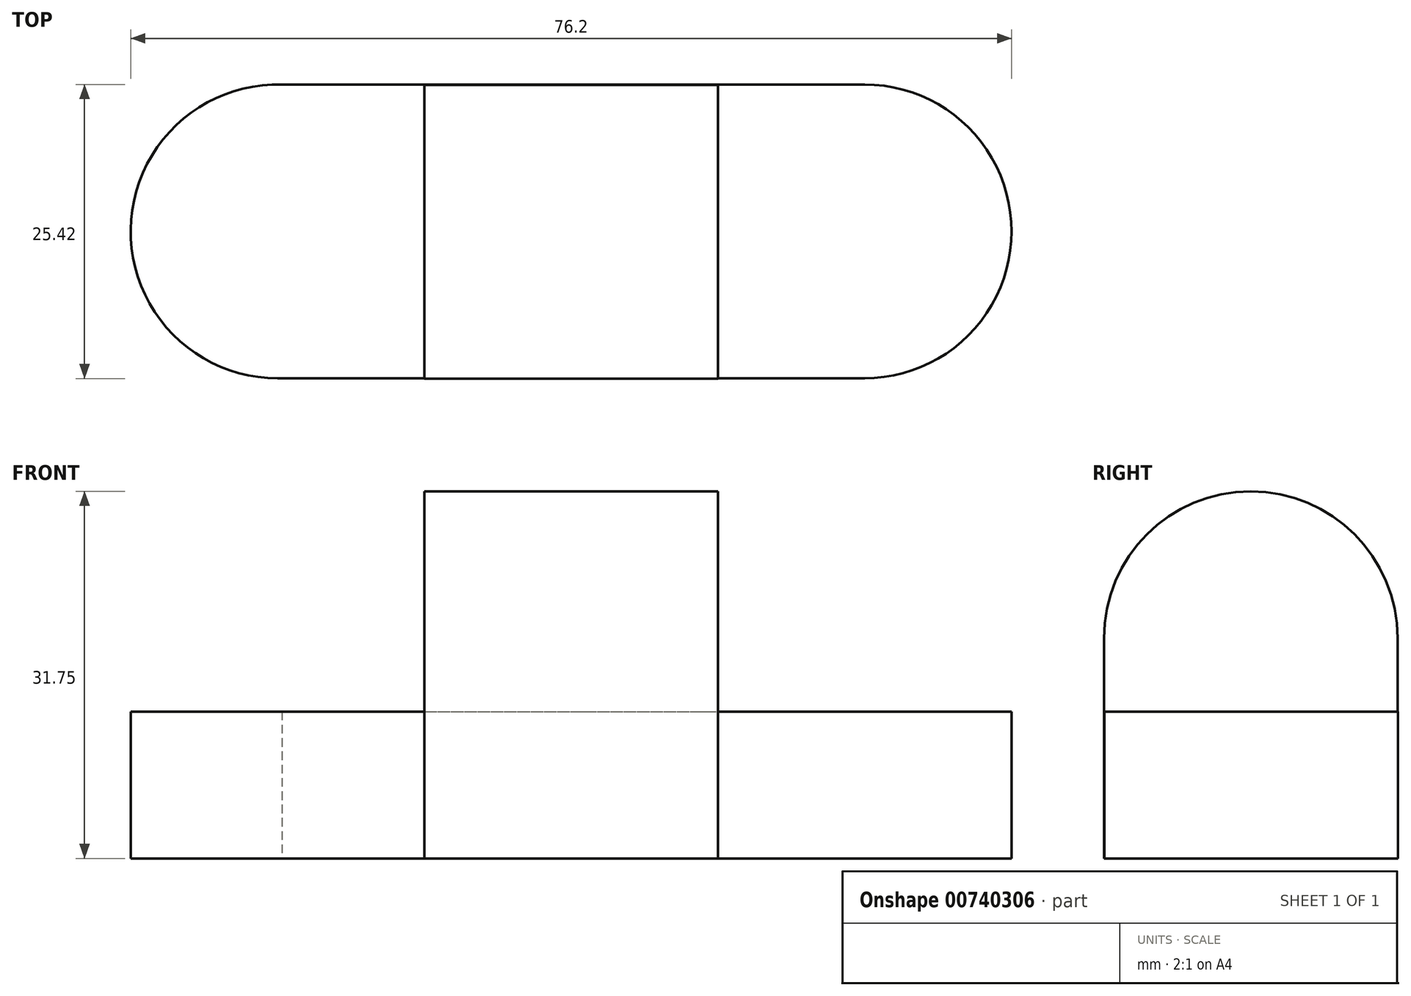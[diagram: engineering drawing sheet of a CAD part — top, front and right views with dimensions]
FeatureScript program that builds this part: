
annotation { "Feature Type Name" : "Feature", "Feature Type Description" : "" }
export const myFeature = defineFeature(function(context is Context, id is Id, definition is map)
    precondition{}
    {
        {
            var Q0;
            Q0=qCreatedBy(makeId("Top.planeOp"),FACE);
            var sketch = newSketch(context, id + "F0", { "sketchPlane" : qUnion([Q0])});
            skCircle(sketch, "E0", {"center": v(-34.8, 0) * mm, "radius": 12.7 * mm});
            skCircle(sketch, "E1", {"center": v(16, 0) * mm, "radius": 12.7 * mm});
            skLineSegment(sketch, "E2", {"start": v(-35.2, 12.7) * mm, "end": v(16, 12.7) * mm});
            skLineSegment(sketch, "E3", {"start": v(-34.8, -12.7) * mm, "end": v(16, -12.7) * mm});
            skSolve(sketch);
        }
        {
            var Q0;
            Q0 = qSketchRegion(id + "F0", true);
            extrude(context, id + "F1", {"entities" : qUnion([Q0]), "depth" : 12.7 * mm, "offsetDistance" : 25.4 * mm});
        }
        {
            var Q0;
            Q0=qCreatedBy(makeId("Top.planeOp"),FACE);
            var sketch = newSketch(context, id + "F2", { "sketchPlane" : qUnion([Q0])});
            skLineSegment(sketch, "E4", {"start": v(-22.1, 12.68) * mm, "end": v(-22.1, -12.72) * mm});
            skLineSegment(sketch, "E5", {"start": v(-22.1, -12.72) * mm, "end": v(3.3, -12.72) * mm});
            skLineSegment(sketch, "E6", {"start": v(3.3, -12.72) * mm, "end": v(3.3, 12.68) * mm});
            skLineSegment(sketch, "E7", {"start": v(3.3, 12.68) * mm, "end": v(-22.1, 12.68) * mm});
            skSolve(sketch);
        }
        {
            var Q0;
            Q0 = qSketchRegion(id + "F2", true);
            extrude(context, id + "F3", {"entities" : qUnion([Q0]), "operationType" : NewBodyOperationType.ADD, "depth" : 19.05 * mm, "offsetDistance" : 25.4 * mm});
        }
        {
            var Q0;
            Q0=makeQuery(id+"F3.opExtrude","SWEPT_FACE",FACE,{"disambiguationData":[OSD([sQuery(id+"F2.wireOp",EDGE,"E6")])]});
            var sketch = newSketch(context, id + "F4", { "sketchPlane" : qUnion([Q0])});
            skArc(sketch, "E8", {"start": v(12.68, 19.05) * mm, "mid": v(-0.02, 31.75) * mm, "end": v(-12.72, 19.05) * mm});
            skSolve(sketch);
        }
        {
            var Q0;
            Q0 = qSketchRegion(id + "F4", true);
            var Q1;
            Q1=makeQuery(id+"F4.imprint","IMPRINT",FACE,{"disambiguationData":[TD([[makeQuery(id+"F4.imprint","IMPRINT",EDGE,{"derivedFrom":sQuery(id+"F4.wireOp",EDGE,"E8")}),1.0]])]});
            extrude(context, id + "F5", {"entities" : qUnion([Q0, Q1]), "operationType" : NewBodyOperationType.ADD, "oppositeDirection" : true, "depth" : 25.4 * mm, "offsetDistance" : 25.4 * mm});
        }
    });
